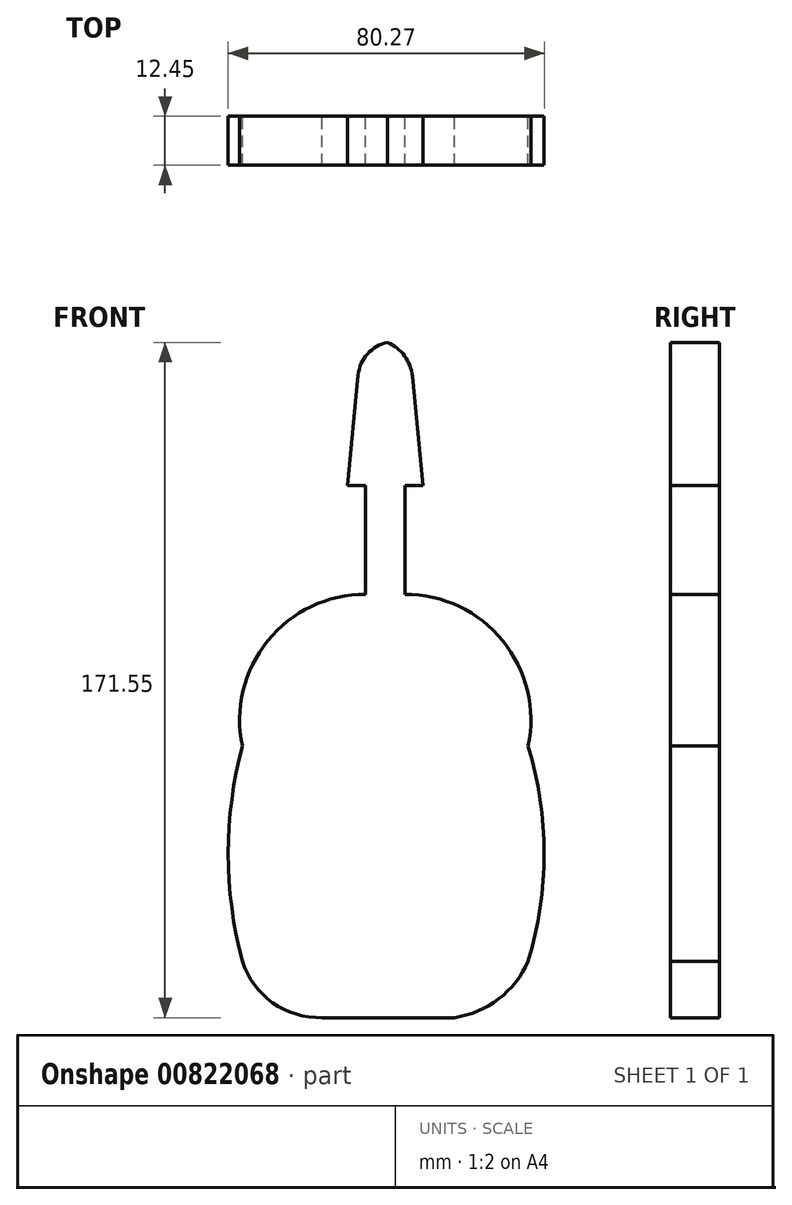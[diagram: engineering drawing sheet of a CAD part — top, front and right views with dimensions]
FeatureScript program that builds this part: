
annotation { "Feature Type Name" : "Feature", "Feature Type Description" : "" }
export const myFeature = defineFeature(function(context is Context, id is Id, definition is map)
    precondition{}
    {
        {
            var Q0;
            Q0=qCreatedBy(makeId("Front.planeOp"),FACE);
            var sketch = newSketch(context, id + "F0", { "sketchPlane" : qUnion([Q0])});
            skLineSegment(sketch, "E0", {"start": v(-10.23, 27.64) * mm, "end": v(-7.48, 55.73) * mm});
            skLineSegment(sketch, "E1", {"start": v(-10.23, 27.64) * mm, "end": v(9, 27.64) * mm});
            skLineSegment(sketch, "E2", {"start": v(9, 27.64) * mm, "end": v(6.26, 55.43) * mm});
            skArc(sketch, "E3", {"start": v(0, 63.98) * mm, "mid": v(-5.1, 61.1) * mm, "end": v(-7.48, 55.73) * mm});
            skArc(sketch, "E4", {"start": v(6.26, 55.43) * mm, "mid": v(4.3, 60.56) * mm, "end": v(0, 63.98) * mm});
            skLineSegment(sketch, "E5", {"start": v(-5.65, 27.64) * mm, "end": v(-5.65, 0) * mm});
            skLineSegment(sketch, "E6", {"start": v(4.43, 27.64) * mm, "end": v(4.43, 0) * mm});
            skLineSegment(sketch, "E7", {"start": v(-5.65, 0) * mm, "end": v(4.43, 0) * mm});
            skLineSegment(sketch, "E8", {"start": v(-36.91, -38.58) * mm, "end": v(35.7, -38.58) * mm});
            skArc(sketch, "E9", {"start": v(-5.65, 0) * mm, "mid": v(-30.48, -11.84) * mm, "end": v(-36.91, -38.58) * mm});
            skArc(sketch, "E10", {"start": v(35.7, -38.58) * mm, "mid": v(29.26, -11.84) * mm, "end": v(4.43, 0) * mm});
            skArc(sketch, "E11", {"start": v(-36.91, -38.58) * mm, "mid": v(-40.5, -65.9) * mm, "end": v(-36.91, -93.2) * mm});
            skArc(sketch, "E12", {"start": v(-36.91, -93.2) * mm, "mid": v(-29.2, -103.77) * mm, "end": v(-16.67, -107.56) * mm});
            skArc(sketch, "E13", {"start": v(35.7, -93.2) * mm, "mid": v(39.77, -65.9) * mm, "end": v(35.7, -38.58) * mm});
            skArc(sketch, "E14", {"start": v(16.98, -107.56) * mm, "mid": v(28.2, -102.82) * mm, "end": v(35.7, -93.2) * mm});
            skLineSegment(sketch, "E15", {"start": v(-16.67, -107.56) * mm, "end": v(16.98, -107.56) * mm});
            skSolve(sketch);
        }
        {
            var Q0;
            {var subQ4=sQuery(id+"F0.wireOp",EDGE,"E0");Q0=makeQuery(id+"F0.imprint","IMPRINT",FACE,{"disambiguationData":[TD([[makeQuery(id+"F0.imprint","IMPRINT",EDGE,{"derivedFrom":subQ4}),-1.0]])]});}
            var Q1;
            {var subQ0=sQuery(id+"F0.wireOp",EDGE,"E5");Q1=makeQuery(id+"F0.imprint","IMPRINT",FACE,{"disambiguationData":[TD([[makeQuery(id+"F0.imprint","IMPRINT",EDGE,{"derivedFrom":subQ0}),1.0]])]});}
            var Q2;
            Q2=makeQuery(id+"F0.imprint","IMPRINT",FACE,{"disambiguationData":[TD([[makeQuery(id+"F0.imprint","IMPRINT",EDGE,{"derivedFrom":sQuery(id+"F0.wireOp",EDGE,"E7")}),-1.0]])]});
            var Q3;
            Q3=makeQuery(id+"F0.imprint","IMPRINT",FACE,{"disambiguationData":[TD([[makeQuery(id+"F0.imprint","IMPRINT",EDGE,{"derivedFrom":sQuery(id+"F0.wireOp",EDGE,"E8")}),-1.0]])]});
            extrude(context, id + "F1", {"entities" : qUnion([Q0, Q1, Q2, Q3]), "depth" : 12.45 * mm, "offsetDistance" : 25.4 * mm});
        }
    });
